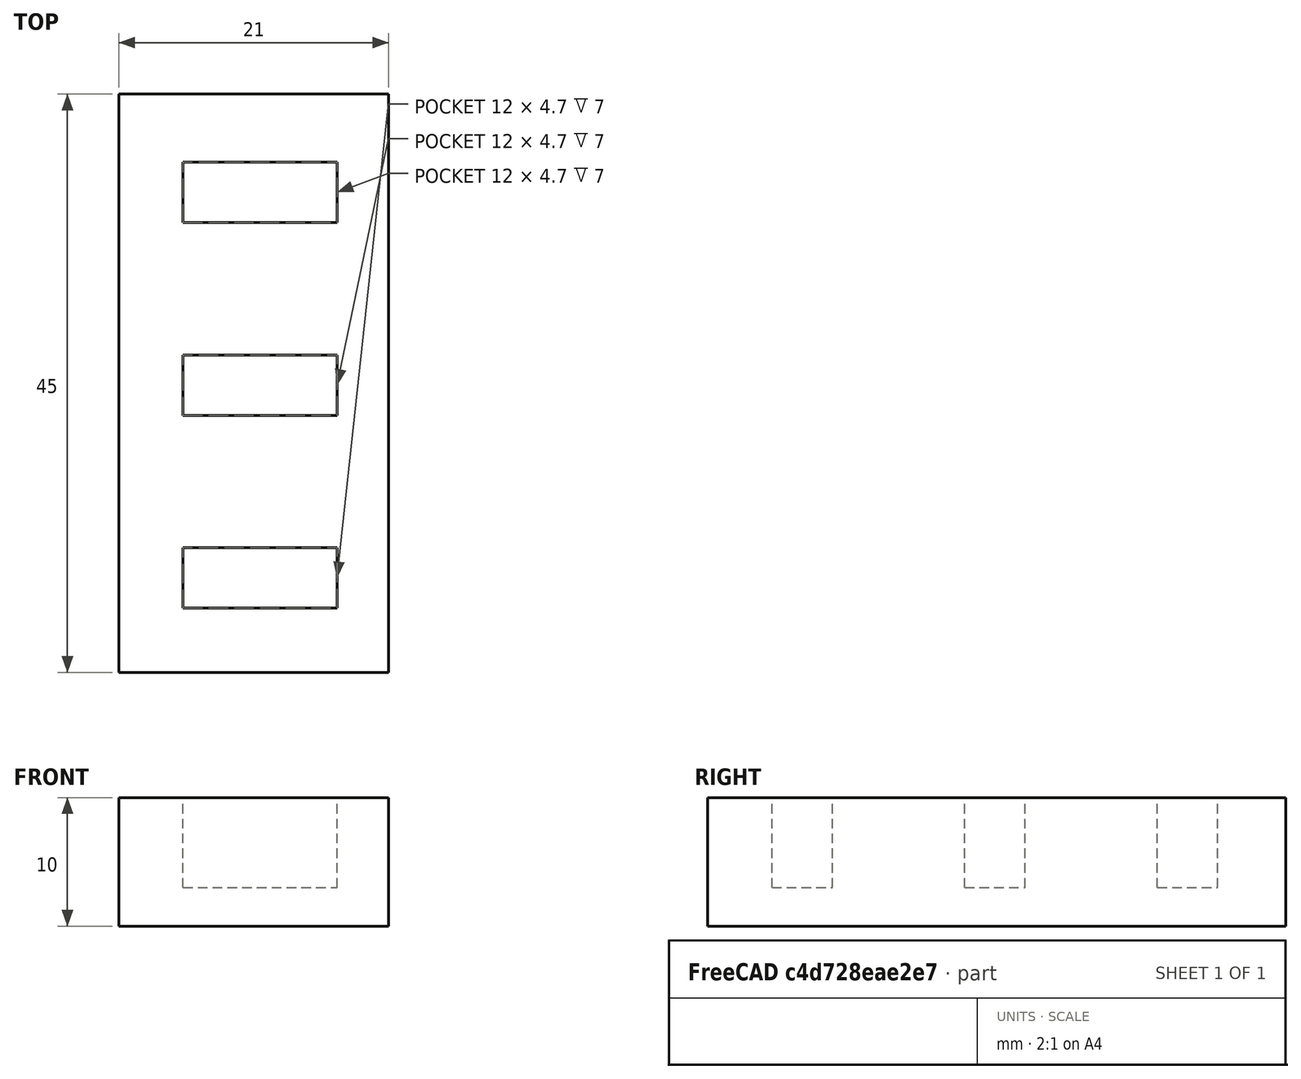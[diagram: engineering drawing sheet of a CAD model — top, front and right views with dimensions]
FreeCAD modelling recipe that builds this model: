
FCSTD DOCUMENT  (FreeCAD 1.0R39319 (Git))
Label: ojt1_t08p01_usb_flash
License: All rights reserved
LicenseURL: https://en.wikipedia.org/wiki/All_rights_reserved
objects: Part::Box×4, Part::MultiFuse×1, Part::Cut×1
note: 6 computed .brp shape members not serialized (recipe doc carries the construction recipe); baked Part::Feature solids carry a one-line shape summary decoded from their .brp

FEATURE [Part::Box] Box  label="Ranura-1"
  AttacherType = Attacher::AttachEngine3D
  Height = 11
  Length = 12
  Width = 4.7
FEATURE [Part::Box] Box001  label="Ranura-002"
  AttacherType = Attacher::AttachEngine3D
  Height = 11
  Length = 12
  Placement = pos=(0,-15,0) rot=(0,0,1;0rad)
  Width = 4.7
FEATURE [Part::Box] Box002  label="Ranura-003"
  AttacherType = Attacher::AttachEngine3D
  Height = 11
  Length = 12
  Placement = pos=(0,15,0) rot=(0,0,1;0rad)
  Width = 4.7
FEATURE [Part::MultiFuse] Fusion
  Placement = pos=(5,20,3) rot=(0,0,1;0rad)
  Refine = true
  Shapes = -> [Box002,Box001,Box]
FEATURE [Part::Box] Box003  label="Cubo"
  AttacherType = Attacher::AttachEngine3D
  Height = 10
  Length = 21
  Width = 45
FEATURE [Part::Cut] Cut  label="Porta-pendrives"
  Base = -> Box003
  Refine = true
  Tool = -> Fusion
